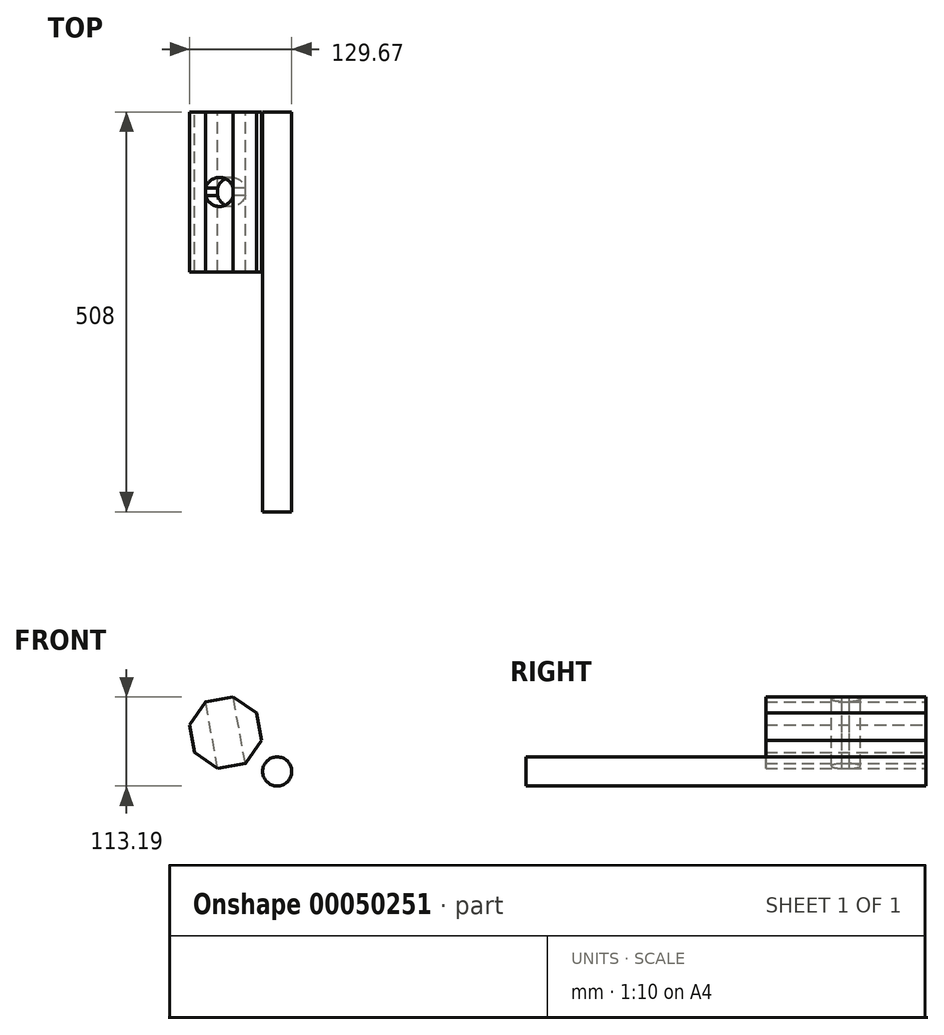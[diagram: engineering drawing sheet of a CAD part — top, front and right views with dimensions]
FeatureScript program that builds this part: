
annotation { "Feature Type Name" : "Feature", "Feature Type Description" : "" }
export const myFeature = defineFeature(function(context is Context, id is Id, definition is map)
    precondition{}
    {
        {
            var Q0;
            Q0=qCreatedBy(makeId("Front.planeOp"),FACE);
            var sketch = newSketch(context, id + "F0", { "sketchPlane" : qUnion([Q0])});
            skCircle(sketch, "E0.cCircle", {"center": v(-89.28, 17.26) * mm, "radius": 43.04 * mm, "construction": true});
            skLineSegment(sketch, "E0.0", {"start": v(-43.75, 7.38) * mm, "end": v(-64.07, -21.92) * mm});
            skLineSegment(sketch, "E0.1", {"start": v(-64.07, -21.92) * mm, "end": v(-99.16, -28.27) * mm});
            skLineSegment(sketch, "E0.2", {"start": v(-99.16, -28.27) * mm, "end": v(-128.46, -7.95) * mm});
            skLineSegment(sketch, "E0.3", {"start": v(-128.46, -7.95) * mm, "end": v(-134.81, 27.14) * mm});
            skLineSegment(sketch, "E0.4", {"start": v(-134.81, 27.14) * mm, "end": v(-114.49, 56.44) * mm});
            skLineSegment(sketch, "E0.5", {"start": v(-114.49, 56.44) * mm, "end": v(-79.4, 62.79) * mm});
            skLineSegment(sketch, "E0.6", {"start": v(-79.4, 62.79) * mm, "end": v(-50.1, 42.47) * mm});
            skLineSegment(sketch, "E0.7", {"start": v(-50.1, 42.47) * mm, "end": v(-43.75, 7.38) * mm});
            skPoint(sketch, "E0.0.midPoint", {"position": v(-53.91, -7.27) * mm});
            skSolve(sketch);
        }
        {
            var Q0;
            Q0 = qSketchRegion(id + "F0", true);
            extrude(context, id + "F1", {"entities" : qUnion([Q0]), "depth" : 203.2 * mm});
        }
        {
            var Q0;
            Q0=makeQuery(id+"F1.opExtrude","SWEPT_FACE",FACE,{"disambiguationData":[OSD([sQuery(id+"F0.wireOp",EDGE,"E0.5")])]});
            var sketch = newSketch(context, id + "F2", { "sketchPlane" : qUnion([Q0])});
            skLineSegment(sketch, "E1.0", {"start": v(-102.61, -203.2) * mm, "end": v(-102.61, 0) * mm});
            skLineSegment(sketch, "E2.0", {"start": v(-66.95, -203.2) * mm, "end": v(-66.95, 0) * mm});
            skLineSegment(sketch, "E3", {"start": v(-102.61, -203.2) * mm, "end": v(-66.95, -203.2) * mm});
            skLineSegment(sketch, "E4", {"start": v(-84.78, -203.2) * mm, "end": v(-84.78, -101.6) * mm});
            skPoint(sketch, "E4.endSnap0", {"position": v(-102.61, -101.6) * mm});
            skCircle(sketch, "E5", {"center": v(-84.78, -101.6) * mm, "radius": 18.48 * mm});
            skSolve(sketch);
        }
        {
            var Q0;
            {var subQ0=sQuery(id+"F2.wireOp",EDGE,"E5");var subQ4=sQuery(id+"F2.wireOp",EDGE,"E1.0");var subQ5=makeQuery(id+"F2.imprint","INTERSECT",VERTEX,{"disambiguationData":[OD(0.0)],"derivedFrom":[subQ4,subQ0]});Q0=makeQuery(id+"F2.imprint","IMPRINT",FACE,{"disambiguationData":[TD([[makeQuery(id+"F2.imprint","IMPRINT",EDGE,{"disambiguationData":[TD([[subQ5,-1.0]])],"derivedFrom":subQ4}),-1.0]])]});}
            extrude(context, id + "F3", {"entities" : qUnion([Q0]), "operationType" : NewBodyOperationType.REMOVE, "oppositeDirection" : true, "depth" : 203.2 * mm});
        }
        {
            var Q0;
            Q0=qCreatedBy(makeId("Front.planeOp"),FACE);
            var sketch = newSketch(context, id + "F4", { "sketchPlane" : qUnion([Q0])});
            skCircle(sketch, "E6", {"center": v(-23.62, -31.92) * mm, "radius": 18.48 * mm});
            skSolve(sketch);
        }
        {
            var Q0;
            Q0=makeQuery(id+"F4.imprint","IMPRINT",FACE,{"disambiguationData":[TD([[makeQuery(id+"F4.imprint","IMPRINT",EDGE,{"derivedFrom":sQuery(id+"F4.wireOp",EDGE,"E6")}),1.0]])]});
            extrude(context, id + "F5", {"entities" : qUnion([Q0]), "depth" : 508 * mm});
        }
    });
